# Revit family: Legrand Colonnes mobiles clippage direct
name_source: partatom
category: Installations électriques
units: mm (PartAtom-declared; Revit-internal decimal feet)

## family parameters
Basée sur le plan de construction = Non
Conserver l'orientation des annotations = Non
Cote de connecteur circulaire = Utiliser le diamètre
Couper avec des vides une fois chargée = Non
Partagée = Non
Point de calcul de pièce = Non
Toujours verticalement = Oui
Type d'élément = Normal

## types (4) — shared parameters
Column Stand type = Pied mobile : Pied pour Colonnettes Blanc
Fabricant = LEGRAND
Matériau principal = Aluminium
Standard = A clippage direct-ON
zero-valued in all types: Elévation par défaut

## per-type parameters (varying)
| type | Column type | Description | Finition | Modèle | Nombre de compartiments | Offset | not Black |
| Colonne 1 cpt 45 2M mobile Blanc | Column - SNAP-ON : Colonne 1 cpt 45 2M mobile Blanc | Colonne mobile a clippage direct 1 compartiment 2m Blanc | Blanc | LG-653006 | 1 compartiment | 10 mm  [stored 0.0328084 ft] | Oui |
| Colonne 1 cpt 45 2M mobile Noir | Column - SNAP-ON : Colonne 1 cpt 45 2M mobile Alu | Colonne mobile a clippage direct 1 compartiment 2m Noir | Noir | LG-653008 | 1 compartiment | 0 mm  [stored 0 ft] | Non |
| Colonne 2 cpt 45 2M mobile Blanc | Column - SNAP-ON : Colonne 2 cpt 45 2M mobile Blanc | Colonne mobile a clippage direct 2 compartiments 2m Blanc | Blanc | LG-653026 | 2 compartiments | 10 mm  [stored 0.0328084 ft] | Oui |
| Colonne 2 cpt 45 2M mobile Noir | Column - SNAP-ON : Colonne 2 cpt 45 2M mobile Noir | Colonne mobile a clippage direct 2 compartiments 2m Noir | Noir | LG-653028 | 2 compartiments | 0 mm  [stored 0 ft] | Non |

note: [stored X ft] marks values corroborated as IEEE doubles in the binary element streams (Revit-internal decimal feet)
